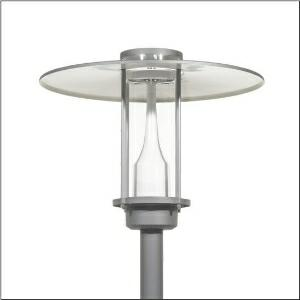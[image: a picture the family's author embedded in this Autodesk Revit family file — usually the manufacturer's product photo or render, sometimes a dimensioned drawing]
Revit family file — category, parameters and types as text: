
# Revit family: city-light_plus_iq___p1_0a_5xa5275lf14hp_bc32
name_source: partatom
category: Lighting Fixtures
units: mm (PartAtom-declared; Revit-internal decimal feet)

## family parameters
Cut with Voids When Loaded = No
Host = Face
Light Source = No
Part Type = Normal
Room Calculation Point = No
Round Connector Dimension = Use Diameter
Shared = No

## types (1)
- --- (1 x LED, 4680 lm, 33.6 W, 4000K)
    Apparent Load = 34 VA
    CIE Flux Codes = 30 60 90 96 100
    Color Rendering = 70
    Color Temperature = 4000K
    Default Elevation = 1800 mm
    Description = City-Light Plus iQ, mast luminaire, Module 540 iQ-SR, primary light control with 3 zone facetted reflector, of plastic, silver coated, highly specular, structured, primary optical cover: cover, of PMMA, transparent, light distribution: P1.0a, light emission: direct distribution, primary light characteristic: strongly asymmetric, installation type: post-top, LED, High Power LED, rated luminous flux: 4.680lm, luminous efficacy: 139lm/W, light colour: 740, colour temperature: 4000K, control gear: iQ Street-Remote, control: pre-setting: logarithmic dimming characteristic, Street-Remote, Auto-Match, Temp-Guard, Lumen-Switch, Night-Set, Smart-Wire, Light-Fading, Desk-Remote (wireless, voltage-free reading and setting of iQ features in the workshop via application-optimized NFC function/RFID function), optimised constant luminous flux control (CLO 2.0), with terminal, 6-pole, max. 2.5mm², mains connection: 230..240V, AC, 50/60Hz, start of lifetime: 34W, end of service life: 36W, reduction: 15W, luminaire housing, upper part, of glass-fibre reinforced polyester, coated, Siteco® metallic grey (DB 702S), diameter: 750mm, height: 590mm, spigot size: d x l = 76 x 70mm (post-top) | with reducer (optional accessory) 60 x 70mm, mounting height: 3..5m, post-top mast mounting element, of diecast aluminium, coated, Siteco® metallic grey (DB 702S), Module 540 iQ-SR, traffic white (RAL 9016), equipment: Power, protection rating (complete): IP65, insulation class (complete): insulation class II (safety insulation), certification: CE, ENEC, VDE, packaging unit: 1 piece

Light Distribution: P1.0a
    Height = 590 mm
    Lamp = 1 x LED
    Lamp Light Flux = 4680 lm
    Lamp Power = 33.6 W
    Lamp count = 1
    Length = 750 mm
    Luminous efficacy = 139 lm/W
    Manufacturer = Siteco
    ModVariant = No
    Model = 5XA5275LF14HP
    Number of Poles = 1
    OnlyDefault = Yes
    Power Factor = 1
    Product Name = City-Light Plus iQ | P1.0a
    Product group = mast luminaire | pylon top
    ProductGroupID = 6100
    Protection Class = Protection class II
    Protection Degree = IP 65
    RLX_Detail_Level = 1
    RLX_Emergency_Light_Flux = 0 lm
    RLX_Emergency_Type = 0
    RLX_Emergency_Type_DB = No
    RlxData = <blob elided: 52545 chars, md5=620fa48f>
    Socket = socket
    Standby Power = 0 W
    System Light Flux = 4680 lm
    System Power = 34 W
    Type Comments = factory setting: luminous flux: 100 % | dim-lin: 254 | 695 mA
    Type Image = l_1006456.jpg
    URL = http://relux.com
    VarID = @adj_191161
    Voltage = 0 V
    Weight = 0.00 kg
    Width = 0 mm  [stored 0 ft]

note: [stored X ft] marks values corroborated as IEEE doubles in the binary element streams (Revit-internal decimal feet)

## geometry (parser evidence)
native form markers: Blend x4, Sweep x12
no freeform markers — native parametric forms only
